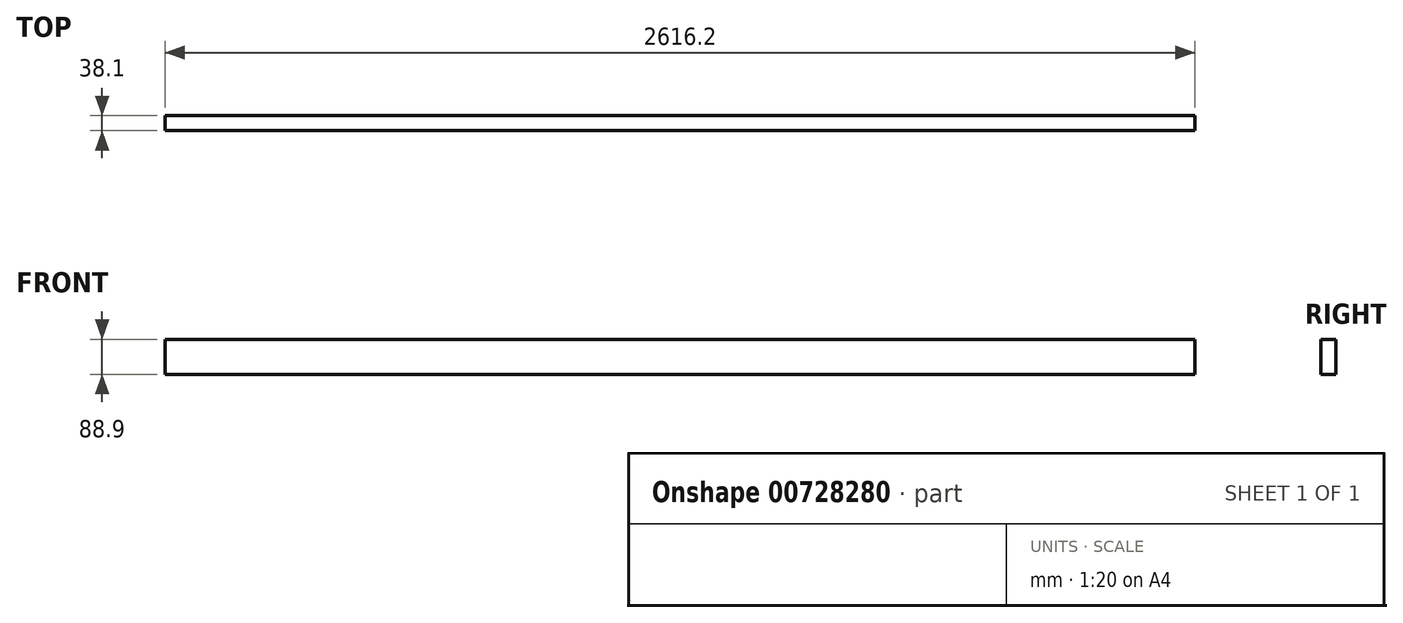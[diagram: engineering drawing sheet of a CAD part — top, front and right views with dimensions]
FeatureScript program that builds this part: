
annotation { "Feature Type Name" : "Feature", "Feature Type Description" : "" }
export const myFeature = defineFeature(function(context is Context, id is Id, definition is map)
    precondition{}
    {
        {
            var Q0;
            Q0=qCreatedBy(makeId("Top.planeOp"),FACE);
            var sketch = newSketch(context, id + "F0", { "sketchPlane" : qUnion([Q0])});
            skLineSegment(sketch, "E0.bottom", {"start": v(-1308.1, -19.05) * mm, "end": v(1308.1, -19.05) * mm});
            skLineSegment(sketch, "E0.top", {"start": v(-1308.1, 19.05) * mm, "end": v(1308.1, 19.05) * mm});
            skLineSegment(sketch, "E0.left", {"start": v(-1308.1, -19.05) * mm, "end": v(-1308.1, 19.05) * mm});
            skLineSegment(sketch, "E0.right", {"start": v(1308.1, -19.05) * mm, "end": v(1308.1, 19.05) * mm});
            skPoint(sketch, "E0.middle", {"position": v(0, 0) * mm});
            skSolve(sketch);
        }
        {
            var Q0;
            Q0=qSketchRegion(id+"F0",true);
            extrude(context, id + "F1", {"entities" : qUnion([Q0]), "depth" : 88.9 * mm, "offsetDistance" : 25.4 * mm});
        }
    });
